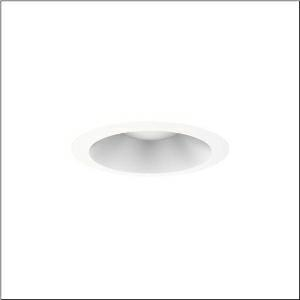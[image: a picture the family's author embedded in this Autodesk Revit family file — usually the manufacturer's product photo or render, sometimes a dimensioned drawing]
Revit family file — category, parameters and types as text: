
# Revit family: lunis_31-xl_51dn15mg42b
name_source: partatom
category: Lighting Fixtures
units: mm (PartAtom-declared; Revit-internal decimal feet)

## family parameters
Cut with Voids When Loaded = No
Host = Face
Light Source = No
Part Type = Normal
Room Calculation Point = No
Round Connector Dimension = Use Diameter
Shared = No

## types (1)
- --- (1 x LED, 2500 lm, 17 W, 4000K)
    Apparent Load = 17 VA
    CIE Flux Codes = 89 99 100 100 100
    Color Rendering = 80
    Color Temperature = 4000K
    Default Elevation = 1800 mm
    Description = Lunis 31, -XL, downlight, light control with lens, light emission: direct distribution, LED rated luminous flux: 2.500lm, light colour: 840, mains connection: 220..240V, AC, 50/60Hz, housing, of aluminium, white, protection rating (complete): IP20, protection rating (on room side): IP54, insulation class (complete): insulation class II (safety insulation), certification: CE, packaging unit: 1 piece
    Height = 0 mm  [stored 0 ft]
    Lamp = 1 x LED
    Lamp Light Flux = 2500 lm
    Lamp Power = 17 W
    Lamp count = 1
    Length = 259 mm
    Luminous efficacy = 147 lm/W
    Manufacturer = Siteco
    ModVariant = No
    Model = 51DN15MG42B
    Mounting Place = Ceiling
    Mounting Type = Recessed
    Number of Poles = 1
    OnlyDefault = Yes
    Power Factor = 1
    Product Name = Lunis 31-XL
    Product group = downlight
    ProductGroupID = 400
    Protection Class = Protection class II
    Protection Degree = IP 20
    RLX_Detail_Level = 1
    RLX_Emergency_Light_Flux = 0 lm
    RLX_Emergency_Type = 0
    RLX_Emergency_Type_DB = No
    RlxData = <blob elided: 24449 chars, md5=b2003a0c>
    Socket = socket
    Standby Power = 0 W
    System Light Flux = 2500 lm
    System Power = 17 W
    Type Comments = individual setting: luminous flux: 100 % | (ON | ON | ON | OFF) | 450 mA
    Type Image = l_1345915.jpg
    URL = http://relux.com
    VarID = @adj_010081
    Voltage = 0 V
    Weight = 0.00 kg
    Width = 0 mm  [stored 0 ft]

note: [stored X ft] marks values corroborated as IEEE doubles in the binary element streams (Revit-internal decimal feet)

## geometry (parser evidence)
native form markers: Blend x4, Sweep x10
no freeform markers — native parametric forms only
